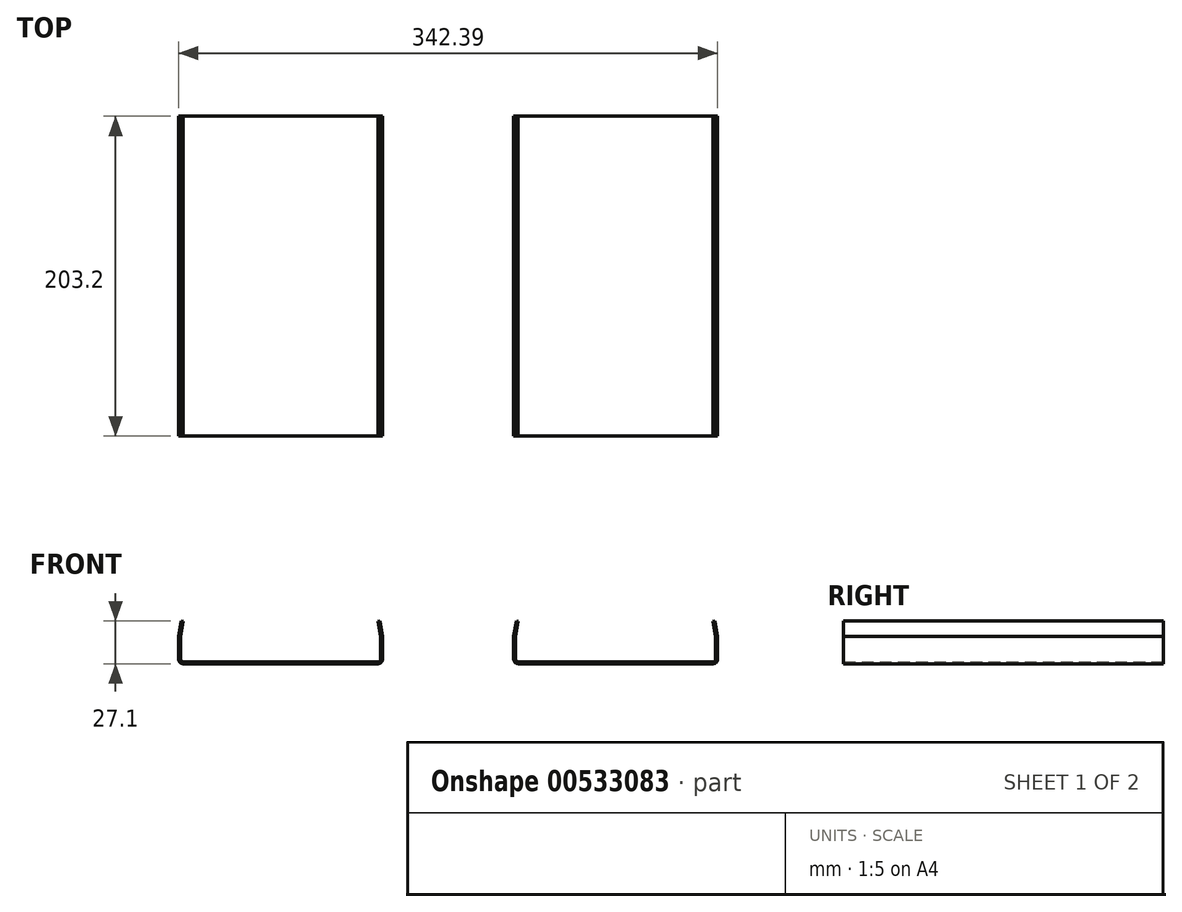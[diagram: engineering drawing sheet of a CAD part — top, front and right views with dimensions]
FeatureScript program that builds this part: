
annotation { "Feature Type Name" : "Feature", "Feature Type Description" : "" }
export const myFeature = defineFeature(function(context is Context, id is Id, definition is map)
    precondition{}
    {
        {
            var Q0;
            Q0=qCreatedBy(makeId("Front.planeOp"),FACE);
            var sketch = newSketch(context, id + "F0", { "sketchPlane" : qUnion([Q0])});
            skLineSegment(sketch, "E0", {"start": v(0, 15.88) * mm, "end": v(0, 1.59) * mm});
            skLineSegment(sketch, "E1", {"start": v(1.59, 0) * mm, "end": v(63.5, 0) * mm});
            skPoint(sketch, "E2.visualSharp", {"position": v(0, 0) * mm});
            skArc(sketch, "E2.filletArc", {"start": v(0, 1.59) * mm, "mid": v(0.46, 0.46) * mm, "end": v(1.59, 0) * mm});
            skLineSegment(sketch, "E3", {"start": v(0, 15.88) * mm, "end": v(1.59, 25.63) * mm});
            skPoint(sketch, "E4.orphan", {"position": v(0, 25.4) * mm});
            skLineSegment(sketch, "E5", {"start": v(63.5, 0) * mm, "end": v(63.5, 38.35) * mm, "construction": true});
            skLineSegment(sketch, "E6.0", {"start": v(-1.27, 15.98) * mm, "end": v(0.33, 25.83) * mm});
            skLineSegment(sketch, "E6.1", {"start": v(-1.27, 15.98) * mm, "end": v(-1.27, 1.59) * mm});
            skArc(sketch, "E6.2", {"start": v(-1.27, 1.59) * mm, "mid": v(-0.43, -0.43) * mm, "end": v(1.59, -1.27) * mm});
            skLineSegment(sketch, "E6.3", {"start": v(1.59, -1.27) * mm, "end": v(63.5, -1.27) * mm});
            skLineSegment(sketch, "E7", {"start": v(0.33, 25.83) * mm, "end": v(1.59, 25.63) * mm});
            skArc(sketch, "E8.MirrorCS", {"start": v(127, 1.59) * mm, "mid": v(126.54, 0.46) * mm, "end": v(125.41, 0) * mm});
            skLineSegment(sketch, "E9.MirrorCS", {"start": v(126.67, 25.83) * mm, "end": v(125.41, 25.63) * mm});
            skArc(sketch, "E10.MirrorCS", {"start": v(128.27, 1.59) * mm, "mid": v(127.43, -0.43) * mm, "end": v(125.41, -1.27) * mm});
            skLineSegment(sketch, "E11.MirrorCS", {"start": v(127, 15.88) * mm, "end": v(127, 1.59) * mm});
            skPoint(sketch, "E12.MirrorP", {"position": v(127, 25.4) * mm});
            skLineSegment(sketch, "E13.MirrorCS", {"start": v(125.41, 0) * mm, "end": v(63.5, 0) * mm});
            skLineSegment(sketch, "E14.MirrorCS", {"start": v(128.27, 15.98) * mm, "end": v(128.27, 1.59) * mm});
            skLineSegment(sketch, "E15.MirrorCS", {"start": v(128.27, 15.98) * mm, "end": v(126.67, 25.83) * mm});
            skPoint(sketch, "E16.MirrorP", {"position": v(127, 0) * mm});
            skLineSegment(sketch, "E17.MirrorCS", {"start": v(125.41, -1.27) * mm, "end": v(63.5, -1.27) * mm});
            skLineSegment(sketch, "E18.MirrorCS", {"start": v(127, 15.88) * mm, "end": v(125.41, 25.63) * mm});
            skSolve(sketch);
        }
        {
            var Q0;
            Q0 = qSketchRegion(id + "F0", true);
            extrude(context, id + "F1", {"entities" : qUnion([Q0]), "depth" : 254 * mm, "offsetDistance" : 25.4 * mm});
        }
        {
            var Q0;
            Q0=makeQuery(id+"F1.opExtrude","SWEPT_FACE",FACE,{"disambiguationData":[OSD([sQuery(id+"F0.wireOp",EDGE,"E6.0")])]});
            var sketch = newSketch(context, id + "F2", { "sketchPlane" : qUnion([Q0])});
            skArc(sketch, "E19", {"start": v(254, 22.37) * mm, "mid": v(253.07, 24.62) * mm, "end": v(250.83, 25.55) * mm});
            skPoint(sketch, "E19.first.point", {"position": v(250.83, 25.55) * mm});
            skPoint(sketch, "E19.second.point", {"position": v(254, 22.37) * mm});
            skPoint(sketch, "E19.third.point", {"position": v(248.33, 20.41) * mm});
            skArc(sketch, "E20", {"start": v(3.17, 25.55) * mm, "mid": v(0.93, 24.62) * mm, "end": v(0, 22.37) * mm});
            skPoint(sketch, "E20.first.point", {"position": v(0, 22.37) * mm});
            skPoint(sketch, "E20.second.point", {"position": v(3.18, 25.55) * mm});
            skPoint(sketch, "E20.third.point", {"position": v(6.07, 21.07) * mm});
            skLineSegment(sketch, "E21.0", {"start": v(254, 25.55) * mm, "end": v(250.83, 25.55) * mm});
            skLineSegment(sketch, "E21.1", {"start": v(0, 22.37) * mm, "end": v(0, 25.55) * mm});
            skLineSegment(sketch, "E21.2", {"start": v(254, 22.37) * mm, "end": v(254, 25.55) * mm});
            skPoint(sketch, "E22.orphan", {"position": v(0, 15.57) * mm});
            skLineSegment(sketch, "E23.trimOffspring", {"start": v(3.18, 25.55) * mm, "end": v(0, 25.55) * mm});
            skPoint(sketch, "E24.orphan", {"position": v(254, 15.57) * mm});
            skSolve(sketch);
        }
        {
            var Q0;
            Q0 = qSketchRegion(id + "F2", true);
            extrude(context, id + "F3", {"entities" : qUnion([Q0]), "operationType" : NewBodyOperationType.REMOVE, "endBound" : BoundingType.UP_TO_NEXT, "oppositeDirection" : true, "depth" : 25.4 * mm, "offsetDistance" : 25.4 * mm});
        }
        {
            var Q0;
            Q0=makeQuery(id+"F1.opExtrude","SWEPT_FACE",FACE,{"disambiguationData":[OSD([sQuery(id+"F0.wireOp",EDGE,"E15.MirrorCS")])]});
            var sketch = newSketch(context, id + "F4", { "sketchPlane" : qUnion([Q0])});
            skArc(sketch, "E25", {"start": v(-250.83, 5.14) * mm, "mid": v(-253.07, 4.2) * mm, "end": v(-254, 1.96) * mm});
            skPoint(sketch, "E25.first.point", {"position": v(-254, 1.96) * mm});
            skPoint(sketch, "E25.second.point", {"position": v(-250.83, 5.14) * mm});
            skPoint(sketch, "E25.third.point", {"position": v(-248.33, 0) * mm});
            skArc(sketch, "E26", {"start": v(0, 1.96) * mm, "mid": v(-0.93, 4.2) * mm, "end": v(-3.18, 5.14) * mm});
            skPoint(sketch, "E26.first.point", {"position": v(-3.18, 5.14) * mm});
            skPoint(sketch, "E26.second.point", {"position": v(0, 1.96) * mm});
            skPoint(sketch, "E26.third.point", {"position": v(-5.38, -0.32) * mm});
            skLineSegment(sketch, "E27.0", {"start": v(-254, 1.96) * mm, "end": v(-254, 5.14) * mm});
            skLineSegment(sketch, "E27.1", {"start": v(-254, 5.14) * mm, "end": v(-250.83, 5.14) * mm});
            skLineSegment(sketch, "E27.2", {"start": v(0, 1.96) * mm, "end": v(0, 5.14) * mm});
            skPoint(sketch, "E28.orphan", {"position": v(-254, -4.84) * mm});
            skLineSegment(sketch, "E29.trimOffspring", {"start": v(-3.18, 5.14) * mm, "end": v(0, 5.14) * mm});
            skPoint(sketch, "E30.orphan", {"position": v(0, -4.84) * mm});
            skSolve(sketch);
        }
        {
            var Q0;
            Q0 = qSketchRegion(id + "F4", true);
            extrude(context, id + "F5", {"entities" : qUnion([Q0]), "operationType" : NewBodyOperationType.REMOVE, "endBound" : BoundingType.UP_TO_NEXT, "oppositeDirection" : true, "depth" : 25.4 * mm, "offsetDistance" : 25.4 * mm});
        }
        {
            var Q0;
            Q0=makeQuery(id+"F1.opExtrude","SWEPT_FACE",FACE,{"disambiguationData":[OSD([sQuery(id+"F0.wireOp",EDGE,"E6.1")])]});
            var sketch = newSketch(context, id + "F6", { "sketchPlane" : qUnion([Q0])});
            skLineSegment(sketch, "E31.bottom", {"start": v(0, 1.59) * mm, "end": v(25.4, 1.59) * mm});
            skLineSegment(sketch, "E31.top", {"start": v(0, 25.83) * mm, "end": v(25.4, 25.83) * mm});
            skLineSegment(sketch, "E31.left", {"start": v(0, 1.59) * mm, "end": v(0, 25.83) * mm});
            skLineSegment(sketch, "E31.right", {"start": v(25.4, 1.59) * mm, "end": v(25.4, 25.83) * mm});
            skLineSegment(sketch, "E32.bottom", {"start": v(254, 1.59) * mm, "end": v(228.6, 1.59) * mm});
            skLineSegment(sketch, "E32.top", {"start": v(254, 25.83) * mm, "end": v(228.6, 25.83) * mm});
            skLineSegment(sketch, "E32.left", {"start": v(254, 1.59) * mm, "end": v(254, 25.83) * mm});
            skLineSegment(sketch, "E32.right", {"start": v(228.6, 1.59) * mm, "end": v(228.6, 25.83) * mm});
            skSolve(sketch);
        }
        {
            var Q0;
            Q0 = qSketchRegion(id + "F6", true);
            extrude(context, id + "F7", {"entities" : qUnion([Q0]), "operationType" : NewBodyOperationType.REMOVE, "endBound" : BoundingType.THROUGH_ALL, "oppositeDirection" : true, "depth" : 25.4 * mm, "offsetDistance" : 25.4 * mm});
        }
        {
            var Q0;
            Q0=makeQuery(id+"F1.opExtrude","SWEPT_BODY",BODY,{"disambiguationData":[OSD([sQuery(id+"F0.wireOp",EDGE,"E0"),sQuery(id+"F0.wireOp",EDGE,"E1"),sQuery(id+"F0.wireOp",EDGE,"E2.filletArc"),sQuery(id+"F0.wireOp",EDGE,"E3"),sQuery(id+"F0.wireOp",EDGE,"E6.0"),sQuery(id+"F0.wireOp",EDGE,"E6.1"),sQuery(id+"F0.wireOp",EDGE,"E6.2"),sQuery(id+"F0.wireOp",EDGE,"E6.3"),sQuery(id+"F0.wireOp",EDGE,"E7"),sQuery(id+"F0.wireOp",EDGE,"E8.MirrorCS"),sQuery(id+"F0.wireOp",EDGE,"E9.MirrorCS"),sQuery(id+"F0.wireOp",EDGE,"E10.MirrorCS"),sQuery(id+"F0.wireOp",EDGE,"E11.MirrorCS"),sQuery(id+"F0.wireOp",EDGE,"E13.MirrorCS"),sQuery(id+"F0.wireOp",EDGE,"E14.MirrorCS"),sQuery(id+"F0.wireOp",EDGE,"E15.MirrorCS"),sQuery(id+"F0.wireOp",EDGE,"E17.MirrorCS"),sQuery(id+"F0.wireOp",EDGE,"E18.MirrorCS")])]});
            transform(context, id + "F8", {"entities" : qUnion([Q0]), "transformType" : TransformType.TRANSLATION_3D, "dx" : -212.85 * mm, "dy" : 0 * mm, "dz" : 0 * mm, "makeCopy" : true});
        }
        {
            var Q0;
            Q0=makeQuery(id+"F8.opPattern","COPY",FACE,{"derivedFrom":makeQuery(id+"F1.opExtrude","SWEPT_FACE",FACE,{"disambiguationData":[OSD([sQuery(id+"F0.wireOp",EDGE,"E6.1")])]}),"instanceName":"1"});
            var sketch = newSketch(context, id + "F9", { "sketchPlane" : qUnion([Q0])});
            skLineSegment(sketch, "E33.bottom", {"start": v(25.4, 1.59) * mm, "end": v(0, 1.59) * mm});
            skLineSegment(sketch, "E33.top", {"start": v(25.4, -1.96) * mm, "end": v(0, -1.96) * mm});
            skLineSegment(sketch, "E33.left", {"start": v(25.4, 1.59) * mm, "end": v(25.4, -1.96) * mm});
            skLineSegment(sketch, "E33.right", {"start": v(0, 1.59) * mm, "end": v(0, -1.96) * mm});
            skLineSegment(sketch, "E34.bottom", {"start": v(228.6, 1.59) * mm, "end": v(254.16, 1.59) * mm});
            skLineSegment(sketch, "E34.top", {"start": v(228.6, -1.66) * mm, "end": v(254.16, -1.66) * mm});
            skLineSegment(sketch, "E34.left", {"start": v(228.6, 1.59) * mm, "end": v(228.6, -1.66) * mm});
            skLineSegment(sketch, "E34.right", {"start": v(254.16, 1.59) * mm, "end": v(254.16, -1.66) * mm});
            skSolve(sketch);
        }
        {
            var Q0;
            Q0 = qSketchRegion(id + "F9", true);
            extrude(context, id + "F10", {"entities" : qUnion([Q0]), "operationType" : NewBodyOperationType.REMOVE, "endBound" : BoundingType.THROUGH_ALL, "oppositeDirection" : true, "depth" : 25.4 * mm, "offsetDistance" : 25.4 * mm});
        }
    });
